# Revit family: Sink_Undermount_Stainless_Steel-Elkay-ELUHAD141445
name_source: partatom
category: Plumbing Fixtures
units: mm (PartAtom-declared; Revit-internal decimal feet)

## family parameters
Cut with Voids When Loaded = No
Host = Face
Maintain Annotation Orientation = No
OmniClass Number = 23.45.05.14.14
OmniClass Title = Sinks/Lavatories
Part Type = Normal
Room Calculation Point = No
Round Connector Dimension = Use Diameter
Shared = No

## types (1)
- ELUHAD141445 (Single Bowl Undermount ADA Sink)
    Approx. Shipping Weight (lbs) = 11
    Assembly Code = D2010.60
    Bowl Length = 14 "
    Bowl Width = 14 "
    Cut Length = 15 "
    Cut width = 15 "
    Default Elevation = 48 "
    Depth of Sink = 4.38 "
    Description = Lustertone Classic Stainless Steel 16 1/2 inch x 16 1/4 inch x 4 3/8 inch Single Bowl Undermount ADA Sink
Single Bowl Undermount ADA Sink w/Perfect Drain
    Drain Location = Rear Center
    Drain Size = 3.5
    Finish = Lustrous Satin
    Gauge = 18
    Installation type = Undermount
    Main Material = Finish-Elkay-Stainless Steel
    Manufacturer = Elkay Manufacturer Company
    Manufacturer Brand = Elkay(Elkay (by Zurn Elkay Water Solutions)
    Masking radius = 2.11 "
    Material = 304 Stainless Steel
    Model = ELUHAD141445
    Outlet Connection Size (inch) = 1.5 "
    Product Documentation Link = https://www.elkayfiles.com
    Product Installation Sheet URL = https://www.elkayfiles.com
    Product Page URL = https://www.elkay.com
    Product Weight (lbs) = 8
    Product data URL = https://www.bimobject.com
    Radius for edge of sink = 2.25 "
    Repair Parts URL = https://www.elkayfiles.com
    Sink Length = 16.5 "
    Sink Width = 16.5 "
    URL = https://www.elkay.com
    Undermount sink = 1 "

## geometry (parser evidence)
native form markers: Sweep x5
no freeform markers — native parametric forms only
